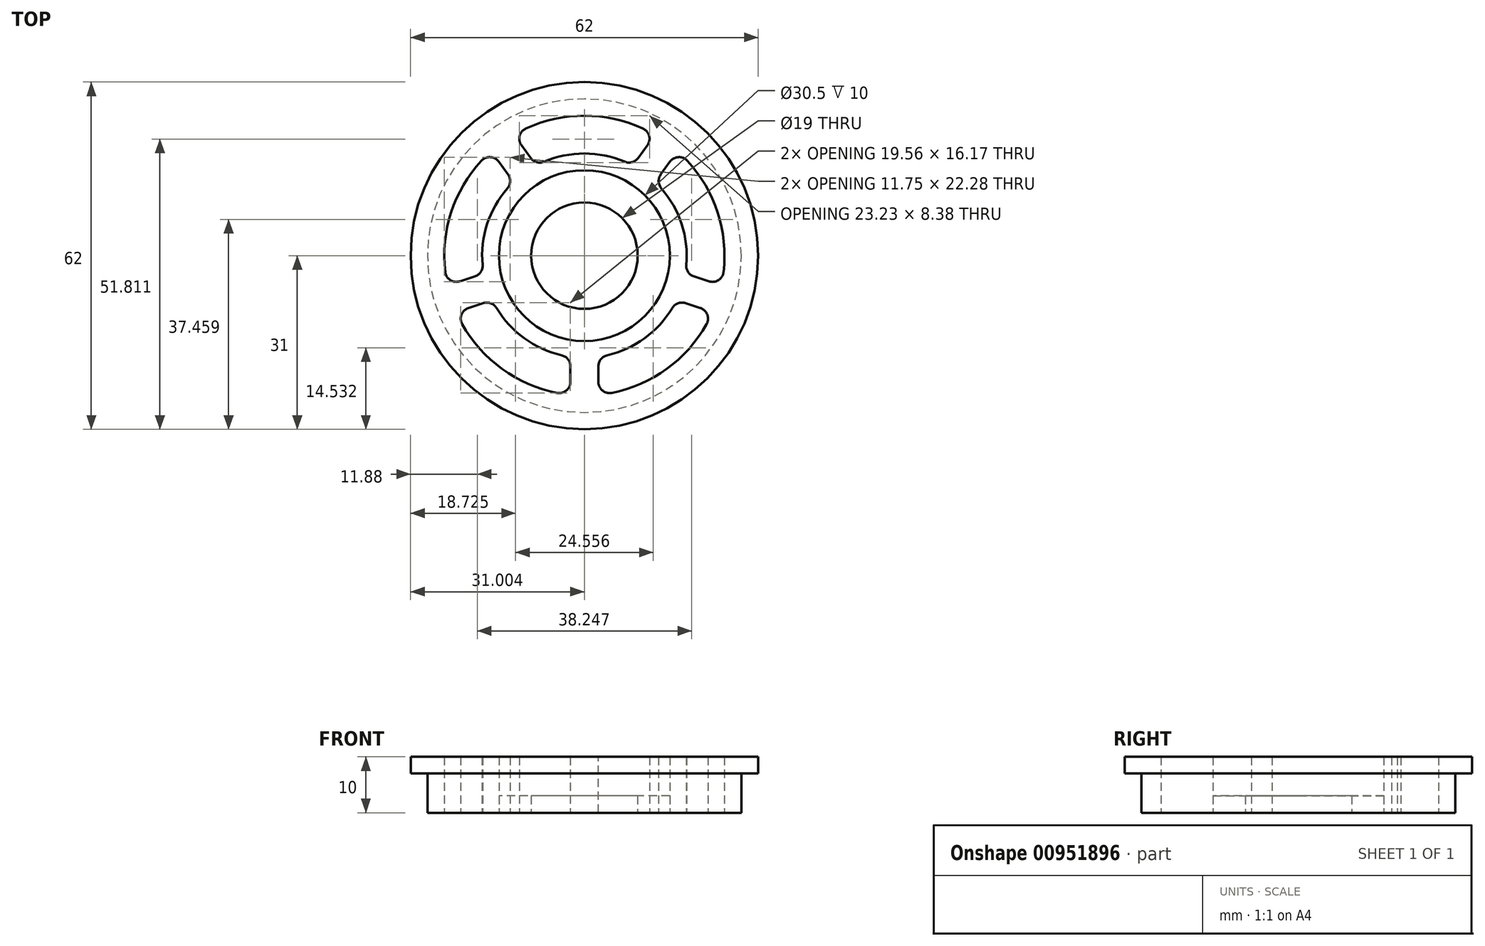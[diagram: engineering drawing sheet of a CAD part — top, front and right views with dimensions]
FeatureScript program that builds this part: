
annotation { "Feature Type Name" : "Feature", "Feature Type Description" : "" }
export const myFeature = defineFeature(function(context is Context, id is Id, definition is map)
    precondition{}
    {
        {
            var Q0;
            Q0=qCreatedBy(makeId("Top.planeOp"),FACE);
            var sketch = newSketch(context, id + "F0", { "sketchPlane" : qUnion([Q0])});
            skCircle(sketch, "E0", {"center": v(-39.15, 0) * mm, "radius": 15.25 * mm});
            skCircle(sketch, "E1", {"center": v(-39.15, 0) * mm, "radius": 28 * mm});
            skCircle(sketch, "E2", {"center": v(-39.15, 0) * mm, "radius": 9.5 * mm});
            skArc(sketch, "E3", {"start": v(-62.03, -10.06) * mm, "mid": v(-53.84, -20.23) * mm, "end": v(-41.65, -24.87) * mm});
            skArc(sketch, "E4", {"start": v(-55.57, -7.96) * mm, "mid": v(-49.87, -14.76) * mm, "end": v(-41.65, -18.08) * mm});
            skLineSegment(sketch, "E5", {"start": v(-41.65, -24.87) * mm, "end": v(-41.65, -18.08) * mm});
            skLineSegment(sketch, "E6", {"start": v(-36.65, -18.08) * mm, "end": v(-36.65, -24.87) * mm});
            skLineSegment(sketch, "E7", {"start": v(-55.57, -7.96) * mm, "end": v(-62.03, -10.06) * mm});
            skLineSegment(sketch, "E8", {"start": v(-57.11, -3.2) * mm, "end": v(-63.58, -5.3) * mm});
            skLineSegment(sketch, "E9", {"start": v(-51.8, 13.16) * mm, "end": v(-55.79, 18.65) * mm});
            skLineSegment(sketch, "E10", {"start": v(-55.79, 18.65) * mm, "end": v(-56.02, 18.38) * mm});
            skLineSegment(sketch, "E11", {"start": v(-47.75, 16.1) * mm, "end": v(-51.74, 21.6) * mm});
            skLineSegment(sketch, "E12", {"start": v(-30.54, 16.1) * mm, "end": v(-26.55, 21.6) * mm});
            skLineSegment(sketch, "E13", {"start": v(-26.5, 13.16) * mm, "end": v(-22.5, 18.65) * mm});
            skLineSegment(sketch, "E14", {"start": v(-21.18, -3.2) * mm, "end": v(-14.72, -5.3) * mm});
            skPoint(sketch, "E14.startSnap0", {"position": v(-21.18, -5.84) * mm});
            skLineSegment(sketch, "E15", {"start": v(-22.73, -7.96) * mm, "end": v(-16.26, -10.06) * mm});
            skPoint(sketch, "E16.orphan", {"position": v(-3.22, -11.67) * mm});
            skArc(sketch, "E17.trimOffspring", {"start": v(-51.8, 13.16) * mm, "mid": v(-56.5, 5.64) * mm, "end": v(-57.11, -3.2) * mm});
            skArc(sketch, "E18.trimOffspring", {"start": v(-55.79, 18.65) * mm, "mid": v(-62.92, 7.73) * mm, "end": v(-63.58, -5.3) * mm});
            skArc(sketch, "E19.trimOffspring", {"start": v(-30.54, 16.1) * mm, "mid": v(-39.15, 18.25) * mm, "end": v(-47.75, 16.1) * mm});
            skArc(sketch, "E20.trimOffspring", {"start": v(-26.55, 21.6) * mm, "mid": v(-39.15, 25) * mm, "end": v(-51.74, 21.6) * mm});
            skArc(sketch, "E21.trimOffspring", {"start": v(-21.18, -3.2) * mm, "mid": v(-21.79, 5.64) * mm, "end": v(-26.5, 13.16) * mm});
            skArc(sketch, "E22.trimOffspring", {"start": v(-14.72, -5.3) * mm, "mid": v(-15.37, 7.73) * mm, "end": v(-22.5, 18.65) * mm});
            skArc(sketch, "E23.trimOffspring", {"start": v(-36.65, -24.87) * mm, "mid": v(-24.45, -20.23) * mm, "end": v(-16.26, -10.06) * mm});
            skArc(sketch, "E24.trimOffspring", {"start": v(-36.65, -18.08) * mm, "mid": v(-28.42, -14.76) * mm, "end": v(-22.73, -7.96) * mm});
            skSolve(sketch);
        }
        {
            var Q0;
            Q0=makeQuery(id+"F0.imprint","IMPRINT",FACE,{"disambiguationData":[TD([[makeQuery(id+"F0.imprint","IMPRINT",EDGE,{"derivedFrom":sQuery(id+"F0.wireOp",EDGE,"E0")}),1.0]])]});
            var Q1;
            Q1=makeQuery(id+"F0.imprint","IMPRINT",FACE,{"disambiguationData":[TD([[makeQuery(id+"F0.imprint","IMPRINT",EDGE,{"derivedFrom":sQuery(id+"F0.wireOp",EDGE,"gZvZpgXt-Y5T6-j4Jx-lpFE-VRuZzmW9fOwK")}),-1.0]])]});
            extrude(context, id + "F1", {"entities" : qUnion([Q0, Q1]), "depth" : 3 * mm, "offsetDistance" : 25 * mm});
        }
        {
            var Q0;
            Q0=makeQuery(id+"F0.imprint","IMPRINT",FACE,{"disambiguationData":[TD([[makeQuery(id+"F0.imprint","IMPRINT",EDGE,{"derivedFrom":sQuery(id+"F0.wireOp",EDGE,"E0")}),-1.0]])]});
            var Q1;
            Q1=makeQuery(id+"F0.imprint","IMPRINT",FACE,{"disambiguationData":[TD([[makeQuery(id+"F0.imprint","IMPRINT",EDGE,{"derivedFrom":sQuery(id+"F0.wireOp",EDGE,"gZvZpgXt-Y5T6-j4Jx-lpFE-VRuZzmW9fOwK")}),1.0]])]});
            extrude(context, id + "F2", {"entities" : qUnion([Q0, Q1]), "depth" : 10 * mm, "offsetDistance" : 25 * mm});
        }
        {
            var Q0;
            Q0=makeQuery(id+"F2.opExtrude","CAP_FACE",FACE,{"disambiguationData":[OSD([sQuery(id+"F0.wireOp",EDGE,"E0"),sQuery(id+"F0.wireOp",EDGE,"E1")])],"isStart":false});
            var sketch = newSketch(context, id + "F3", { "sketchPlane" : qUnion([Q0])});
            skCircle(sketch, "E25", {"center": v(-39.15, 0) * mm, "radius": 31 * mm});
            skSolve(sketch);
        }
        {
            var Q0;
            Q0=makeQuery(id+"F3.imprint","IMPRINT",FACE,{"disambiguationData":[TD([[makeQuery(id+"F3.imprint","IMPRINT",EDGE,{"derivedFrom":sQuery(id+"F3.wireOp",EDGE,"E25")}),1.0]])]});
            extrude(context, id + "F4", {"entities" : qUnion([Q0]), "operationType" : NewBodyOperationType.ADD, "oppositeDirection" : true, "depth" : 3 * mm, "offsetDistance" : 25 * mm});
        }
        {
            var Q0;
            Q0=makeQuery(id+"F2.opExtrude","SWEPT_EDGE",EDGE,{"disambiguationData":[OSD([sQuery(id+"F0.wireOp",EDGE,"E3"),sQuery(id+"F0.wireOp",EDGE,"E7")])]});
            var Q1;
            Q1=makeQuery(id+"F2.opExtrude","SWEPT_EDGE",EDGE,{"disambiguationData":[OSD([sQuery(id+"F0.wireOp",EDGE,"E4"),sQuery(id+"F0.wireOp",EDGE,"E7")])]});
            var Q2;
            Q2=makeQuery(id+"F2.opExtrude","SWEPT_EDGE",EDGE,{"disambiguationData":[OSD([sQuery(id+"F0.wireOp",EDGE,"E3"),sQuery(id+"F0.wireOp",EDGE,"E5")])]});
            var Q3;
            Q3=makeQuery(id+"F2.opExtrude","SWEPT_EDGE",EDGE,{"disambiguationData":[OSD([sQuery(id+"F0.wireOp",EDGE,"E4"),sQuery(id+"F0.wireOp",EDGE,"E5")])]});
            var Q4;
            Q4=makeQuery(id+"F2.opExtrude","SWEPT_EDGE",EDGE,{"disambiguationData":[OSD([sQuery(id+"F0.wireOp",EDGE,"E6"),sQuery(id+"F0.wireOp",EDGE,"E24.trimOffspring")])]});
            var Q5;
            Q5=makeQuery(id+"F2.opExtrude","SWEPT_EDGE",EDGE,{"disambiguationData":[OSD([sQuery(id+"F0.wireOp",EDGE,"E6"),sQuery(id+"F0.wireOp",EDGE,"E23.trimOffspring")])]});
            var Q6;
            Q6=makeQuery(id+"F2.opExtrude","SWEPT_EDGE",EDGE,{"disambiguationData":[OSD([sQuery(id+"F0.wireOp",EDGE,"E15"),sQuery(id+"F0.wireOp",EDGE,"E23.trimOffspring")])]});
            var Q7;
            Q7=makeQuery(id+"F2.opExtrude","SWEPT_EDGE",EDGE,{"disambiguationData":[OSD([sQuery(id+"F0.wireOp",EDGE,"E15"),sQuery(id+"F0.wireOp",EDGE,"E24.trimOffspring")])]});
            var Q8;
            Q8=makeQuery(id+"F2.opExtrude","SWEPT_EDGE",EDGE,{"disambiguationData":[OSD([sQuery(id+"F0.wireOp",EDGE,"E14"),sQuery(id+"F0.wireOp",EDGE,"E22.trimOffspring")])]});
            var Q9;
            Q9=makeQuery(id+"F2.opExtrude","SWEPT_EDGE",EDGE,{"disambiguationData":[OSD([sQuery(id+"F0.wireOp",EDGE,"E14"),sQuery(id+"F0.wireOp",EDGE,"E21.trimOffspring")])]});
            var Q10;
            Q10=makeQuery(id+"F2.opExtrude","SWEPT_EDGE",EDGE,{"disambiguationData":[OSD([sQuery(id+"F0.wireOp",EDGE,"E13"),sQuery(id+"F0.wireOp",EDGE,"E21.trimOffspring")])]});
            var Q11;
            Q11=makeQuery(id+"F2.opExtrude","SWEPT_EDGE",EDGE,{"disambiguationData":[OSD([sQuery(id+"F0.wireOp",EDGE,"E13"),sQuery(id+"F0.wireOp",EDGE,"E22.trimOffspring")])]});
            var Q12;
            Q12=makeQuery(id+"F2.opExtrude","SWEPT_EDGE",EDGE,{"disambiguationData":[OSD([sQuery(id+"F0.wireOp",EDGE,"E12"),sQuery(id+"F0.wireOp",EDGE,"E20.trimOffspring")])]});
            var Q13;
            Q13=makeQuery(id+"F2.opExtrude","SWEPT_EDGE",EDGE,{"disambiguationData":[OSD([sQuery(id+"F0.wireOp",EDGE,"E12"),sQuery(id+"F0.wireOp",EDGE,"E19.trimOffspring")])]});
            var Q14;
            Q14=makeQuery(id+"F2.opExtrude","SWEPT_EDGE",EDGE,{"disambiguationData":[OSD([sQuery(id+"F0.wireOp",EDGE,"E11"),sQuery(id+"F0.wireOp",EDGE,"E19.trimOffspring")])]});
            var Q15;
            Q15=makeQuery(id+"F2.opExtrude","SWEPT_EDGE",EDGE,{"disambiguationData":[OSD([sQuery(id+"F0.wireOp",EDGE,"E11"),sQuery(id+"F0.wireOp",EDGE,"E20.trimOffspring")])]});
            var Q16;
            Q16=makeQuery(id+"F2.opExtrude","SWEPT_EDGE",EDGE,{"disambiguationData":[OSD([sQuery(id+"F0.wireOp",EDGE,"E9"),sQuery(id+"F0.wireOp",EDGE,"E17.trimOffspring")])]});
            var Q17;
            Q17=makeQuery(id+"F2.opExtrude","SWEPT_EDGE",EDGE,{"disambiguationData":[OSD([sQuery(id+"F0.wireOp",EDGE,"E8"),sQuery(id+"F0.wireOp",EDGE,"E17.trimOffspring")])]});
            var Q18;
            Q18=makeQuery(id+"F2.opExtrude","SWEPT_EDGE",EDGE,{"disambiguationData":[OSD([sQuery(id+"F0.wireOp",EDGE,"E8"),sQuery(id+"F0.wireOp",EDGE,"E18.trimOffspring")])]});
            var Q19;
            Q19=makeQuery(id+"F2.opExtrude","SWEPT_EDGE",EDGE,{"disambiguationData":[OSD([sQuery(id+"F0.wireOp",EDGE,"E9"),sQuery(id+"F0.wireOp",EDGE,"E18.trimOffspring")])]});
            fillet(context, id + "F5", {"entities" : qUnion([Q0, Q1, Q2, Q3, Q4, Q5, Q6, Q7, Q8, Q9, Q10, Q11, Q12, Q13, Q14, Q15, Q16, Q17, Q18, Q19]), "radius" : 2 * mm, "tangentPropagation" : true, "allowEdgeOverflow" : false});
        }
    });
